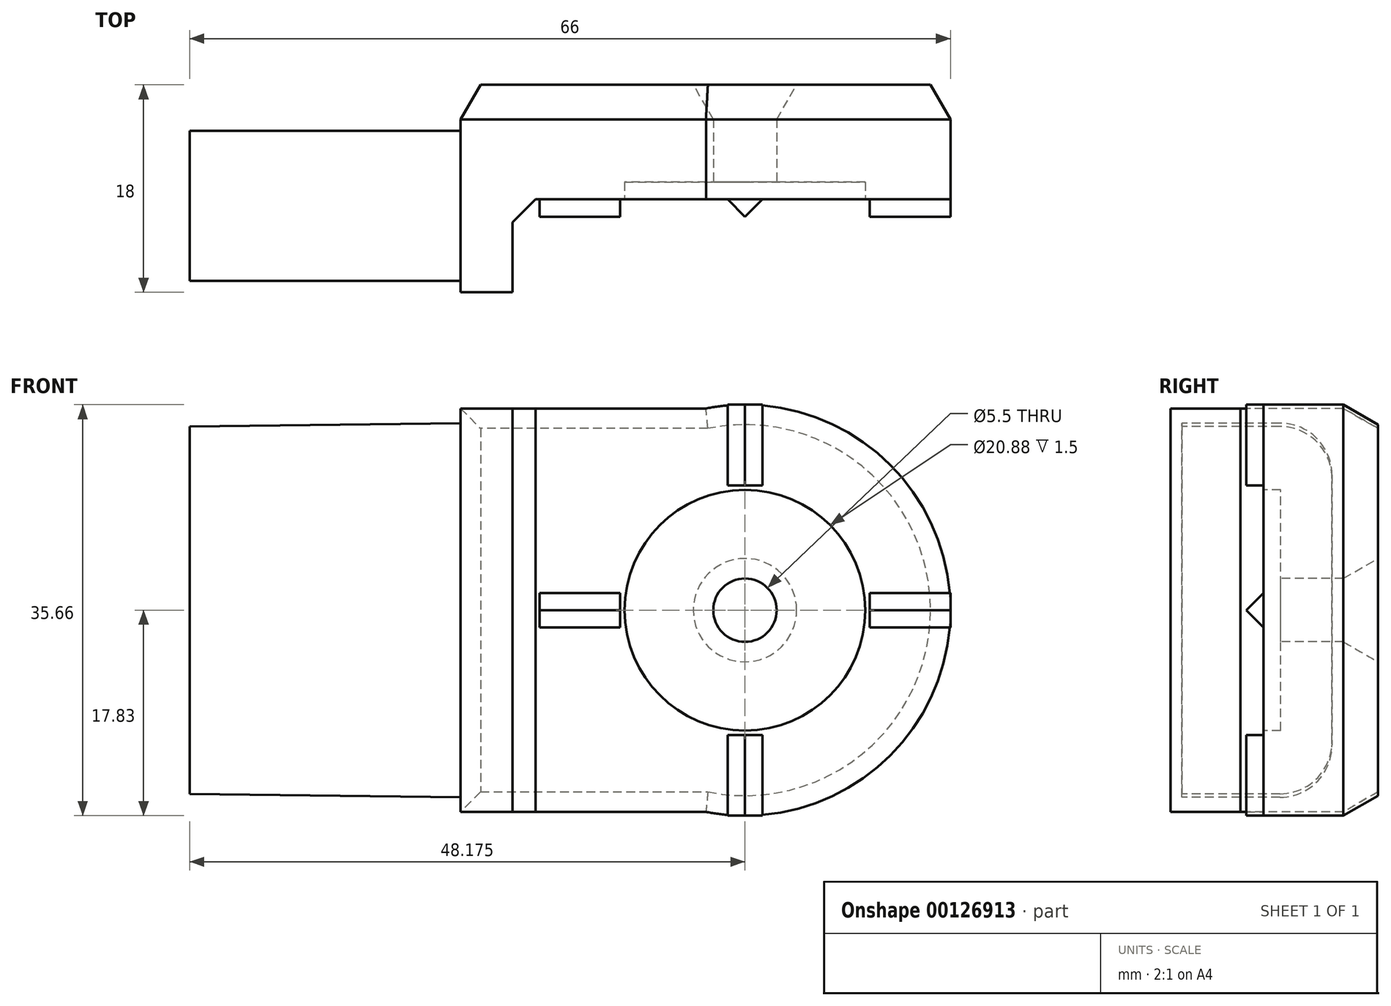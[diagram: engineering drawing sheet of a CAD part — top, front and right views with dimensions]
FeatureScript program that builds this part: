
annotation { "Feature Type Name" : "Feature", "Feature Type Description" : "" }
export const myFeature = defineFeature(function(context is Context, id is Id, definition is map)
    precondition{}
    {
        {
            var Q0;
            Q0=qCreatedBy(makeId("Front.planeOp"),FACE);
            var sketch = newSketch(context, id + "F0", { "sketchPlane" : qUnion([Q0])});
            skLineSegment(sketch, "E0.bottom", {"start": v(-32.5, 17.5) * mm, "end": v(32.5, 17.5) * mm});
            skLineSegment(sketch, "E0.top", {"start": v(-32.5, -17.5) * mm, "end": v(32.5, -17.5) * mm});
            skLineSegment(sketch, "E0.left", {"start": v(-32.5, 17.5) * mm, "end": v(-32.5, -17.5) * mm});
            skLineSegment(sketch, "E0.right", {"start": v(32.5, 17.5) * mm, "end": v(32.5, -17.5) * mm});
            skSolve(sketch);
        }
        {
            var Q0;
            Q0=makeQuery(id+"F0.imprint","IMPRINT",FACE,{"disambiguationData":[TD([[makeQuery(id+"F0.imprint","IMPRINT",EDGE,{"derivedFrom":sQuery(id+"F0.wireOp",EDGE,"E0.bottom")}),-1.0]])]});
            extrude(context, id + "F1", {"entities" : qUnion([Q0]), "depth" : 15 * mm});
        }
        {
            var Q0;
            Q0=makeQuery(id+"F1.opExtrude","CAP_FACE",FACE,{"disambiguationData":[OSD([sQuery(id+"F0.wireOp",EDGE,"E0.bottom"),sQuery(id+"F0.wireOp",EDGE,"E0.top"),sQuery(id+"F0.wireOp",EDGE,"E0.left"),sQuery(id+"F0.wireOp",EDGE,"E0.right")])],"isStart":false});
            var sketch = newSketch(context, id + "F2", { "sketchPlane" : qUnion([Q0])});
            skCircle(sketch, "E1", {"center": v(15.68, 0) * mm, "radius": 17.82 * mm});
            skSolve(sketch);
        }
        {
            var Q0;
            Q0 = qSketchRegion(id + "F2", true);
            var Q1;
            Q1=makeQuery(id+"F1.opExtrude","CAP_FACE",FACE,{"disambiguationData":[OSD([sQuery(id+"F0.wireOp",EDGE,"E0.bottom"),sQuery(id+"F0.wireOp",EDGE,"E0.top"),sQuery(id+"F0.wireOp",EDGE,"E0.left"),sQuery(id+"F0.wireOp",EDGE,"E0.right")])],"isStart":true});
            extrude(context, id + "F3", {"entities" : qUnion([Q0]), "operationType" : NewBodyOperationType.ADD, "endBound" : BoundingType.UP_TO_SURFACE, "oppositeDirection" : true, "endBoundEntityFace" : qUnion([Q1]), "depth" : 25 * mm});
        }
        {
            var Q0;
            Q0=makeQuery(id+"F3.boolean.opBoolean","MERGE",FACE,{"derivedFrom":[makeQuery(id+"F1.opExtrude","CAP_FACE",FACE,{"disambiguationData":[OSD([sQuery(id+"F0.wireOp",EDGE,"E0.bottom"),sQuery(id+"F0.wireOp",EDGE,"E0.top"),sQuery(id+"F0.wireOp",EDGE,"E0.left"),sQuery(id+"F0.wireOp",EDGE,"E0.right")])],"isStart":false}),makeQuery(id+"F3.opExtrude","CAP_FACE",FACE,{"disambiguationData":[OSD([sQuery(id+"F2.wireOp",EDGE,"E1")])],"isStart":true})]});
            var sketch = newSketch(context, id + "F4", { "sketchPlane" : qUnion([Q0])});
            skLineSegment(sketch, "E2.bottom", {"start": v(-4.5, -18.83) * mm, "end": v(34.5, -18.83) * mm});
            skLineSegment(sketch, "E2.top", {"start": v(-4.5, 18.83) * mm, "end": v(34.5, 18.83) * mm});
            skLineSegment(sketch, "E2.left", {"start": v(-4.5, -18.83) * mm, "end": v(-4.5, 18.83) * mm});
            skLineSegment(sketch, "E2.right", {"start": v(34.5, -18.83) * mm, "end": v(34.5, 18.83) * mm});
            skSolve(sketch);
        }
        {
            var Q0;
            Q0 = qSketchRegion(id + "F4", true);
            extrude(context, id + "F5", {"entities" : qUnion([Q0]), "operationType" : NewBodyOperationType.REMOVE, "oppositeDirection" : true, "depth" : 8.06 * mm});
        }
        {
            var Q0;
            Q0=makeQuery(id+"F3.boolean.opBoolean","MERGE",FACE,{"derivedFrom":[makeQuery(id+"F1.opExtrude","CAP_FACE",FACE,{"disambiguationData":[OSD([sQuery(id+"F0.wireOp",EDGE,"E0.bottom"),sQuery(id+"F0.wireOp",EDGE,"E0.top"),sQuery(id+"F0.wireOp",EDGE,"E0.left"),sQuery(id+"F0.wireOp",EDGE,"E0.right")])],"isStart":false}),makeQuery(id+"F3.opExtrude","CAP_FACE",FACE,{"disambiguationData":[OSD([sQuery(id+"F2.wireOp",EDGE,"E1")])],"isStart":true})]});
            var sketch = newSketch(context, id + "F6", { "sketchPlane" : qUnion([Q0])});
            skLineSegment(sketch, "E3", {"start": v(-9, -17.5) * mm, "end": v(-9, 17.5) * mm, "construction": true});
            skLineSegment(sketch, "E4", {"start": v(-9, 17.5) * mm, "end": v(-32.5, 17.5) * mm});
            skLineSegment(sketch, "E5", {"start": v(-32.5, 17.5) * mm, "end": v(-32.5, 15.93) * mm});
            skLineSegment(sketch, "E6", {"start": v(-32.5, 15.93) * mm, "end": v(-9, 16.23) * mm});
            skLineSegment(sketch, "E7", {"start": v(-9, 16.23) * mm, "end": v(-9, 17.5) * mm});
            skLineSegment(sketch, "E8", {"start": v(-9, -17.5) * mm, "end": v(-32.5, -17.5) * mm});
            skLineSegment(sketch, "E9", {"start": v(-32.5, -17.5) * mm, "end": v(-32.5, -15.93) * mm});
            skLineSegment(sketch, "E10", {"start": v(-32.5, -15.93) * mm, "end": v(-9, -16.23) * mm});
            skLineSegment(sketch, "E11", {"start": v(-9, -16.23) * mm, "end": v(-9, -17.5) * mm});
            skSolve(sketch);
        }
        {
            var Q0;
            Q0 = qSketchRegion(id + "F6", true);
            extrude(context, id + "F7", {"entities" : qUnion([Q0]), "operationType" : NewBodyOperationType.REMOVE, "endBound" : BoundingType.THROUGH_ALL, "oppositeDirection" : true, "depth" : 25 * mm});
        }
        {
            var Q0;
            Q0=makeQuery(id+"F3.boolean.opBoolean","MERGE",FACE,{"derivedFrom":[makeQuery(id+"F1.opExtrude","CAP_FACE",FACE,{"disambiguationData":[OSD([sQuery(id+"F0.wireOp",EDGE,"E0.bottom"),sQuery(id+"F0.wireOp",EDGE,"E0.top"),sQuery(id+"F0.wireOp",EDGE,"E0.left"),sQuery(id+"F0.wireOp",EDGE,"E0.right")])],"isStart":false}),makeQuery(id+"F3.opExtrude","CAP_FACE",FACE,{"disambiguationData":[OSD([sQuery(id+"F2.wireOp",EDGE,"E1")])],"isStart":true})]});
            var sketch = newSketch(context, id + "F8", { "sketchPlane" : qUnion([Q0])});
            skLineSegment(sketch, "E12.bottom", {"start": v(-9, -17.5) * mm, "end": v(-39.86, -17.5) * mm});
            skLineSegment(sketch, "E12.top", {"start": v(-9, 20.06) * mm, "end": v(-39.86, 20.06) * mm});
            skLineSegment(sketch, "E12.left", {"start": v(-9, -17.5) * mm, "end": v(-9, 20.06) * mm});
            skLineSegment(sketch, "E12.right", {"start": v(-39.86, -17.5) * mm, "end": v(-39.86, 20.06) * mm});
            skSolve(sketch);
        }
        {
            var Q0;
            Q0 = qSketchRegion(id + "F8", true);
            extrude(context, id + "F9", {"entities" : qUnion([Q0]), "operationType" : NewBodyOperationType.REMOVE, "oppositeDirection" : true, "depth" : 1 * mm});
        }
        {
            var Q0;
            {var subQ0=sQuery(id+"F0.wireOp",EDGE,"E0.right");var subQ1=sQuery(id+"F0.wireOp",EDGE,"E0.left");var subQ2=sQuery(id+"F0.wireOp",EDGE,"E0.top");var subQ3=sQuery(id+"F0.wireOp",EDGE,"E0.bottom");Q0=makeQuery(id+"F3.boolean.opBoolean","MERGE",FACE,{"derivedFrom":[makeQuery(id+"F1.opExtrude","CAP_FACE",FACE,{"disambiguationData":[OSD([subQ3,subQ2,subQ1,subQ0])],"isStart":true}),makeQuery(id+"F3.opExtrude","CAP_FACE",FACE,{"disambiguationData":[OSD([subQ3,subQ2,subQ1,subQ0])],"isStart":false})]});}
            var sketch = newSketch(context, id + "F10", { "sketchPlane" : qUnion([Q0])});
            skLineSegment(sketch, "E13.bottom", {"start": v(9, -17.5) * mm, "end": v(34.5, -17.5) * mm});
            skLineSegment(sketch, "E13.top", {"start": v(9, 17.5) * mm, "end": v(34.5, 17.5) * mm});
            skLineSegment(sketch, "E13.left", {"start": v(9, -17.5) * mm, "end": v(9, 17.5) * mm});
            skLineSegment(sketch, "E13.right", {"start": v(34.5, -17.5) * mm, "end": v(34.5, 17.5) * mm});
            skSolve(sketch);
        }
        {
            var Q0;
            Q0 = qSketchRegion(id + "F10", true);
            extrude(context, id + "F11", {"entities" : qUnion([Q0]), "operationType" : NewBodyOperationType.REMOVE, "oppositeDirection" : true, "depth" : 1 * mm});
        }
        {
            var Q0;
            Q0=makeQuery(id+"F5.boolean.opBoolean","COPY",EDGE,{"derivedFrom":makeQuery(id+"F5.opExtrude","CAP_EDGE",EDGE,{"disambiguationData":[OSD([sQuery(id+"F4.wireOp",EDGE,"E2.left")])],"isStart":false})});
            chamfer(context, id + "F12", {"entities" : qUnion([Q0]), "width" : 2 * mm, "tangentPropagation" : true});
        }
        {
            var Q0;
            Q0=makeQuery(id+"F5.boolean.opBoolean","COPY",FACE,{"derivedFrom":makeQuery(id+"F5.opExtrude","CAP_FACE",FACE,{"disambiguationData":[OSD([sQuery(id+"F4.wireOp",EDGE,"E2.bottom"),sQuery(id+"F4.wireOp",EDGE,"E2.top"),sQuery(id+"F4.wireOp",EDGE,"E2.left"),sQuery(id+"F4.wireOp",EDGE,"E2.right")])],"isStart":false})});
            var sketch = newSketch(context, id + "F13", { "sketchPlane" : qUnion([Q0])});
            skCircle(sketch, "E14", {"center": v(15.68, 0) * mm, "radius": 2.75 * mm});
            skSolve(sketch);
        }
        {
            var Q0;
            Q0 = qSketchRegion(id + "F13", true);
            extrude(context, id + "F14", {"entities" : qUnion([Q0]), "operationType" : NewBodyOperationType.REMOVE, "endBound" : BoundingType.THROUGH_ALL, "oppositeDirection" : true, "depth" : 25 * mm});
        }
        {
            var Q0;
            Q0=makeQuery(id+"F5.boolean.opBoolean","COPY",FACE,{"derivedFrom":makeQuery(id+"F5.opExtrude","CAP_FACE",FACE,{"disambiguationData":[OSD([sQuery(id+"F4.wireOp",EDGE,"E2.bottom"),sQuery(id+"F4.wireOp",EDGE,"E2.top"),sQuery(id+"F4.wireOp",EDGE,"E2.left"),sQuery(id+"F4.wireOp",EDGE,"E2.right")])],"isStart":false})});
            var sketch = newSketch(context, id + "F15", { "sketchPlane" : qUnion([Q0])});
            skCircle(sketch, "E15", {"center": v(15.68, 0) * mm, "radius": 10.44 * mm});
            skSolve(sketch);
        }
        {
            var Q0;
            Q0 = qSketchRegion(id + "F15", true);
            extrude(context, id + "F16", {"entities" : qUnion([Q0]), "operationType" : NewBodyOperationType.REMOVE, "oppositeDirection" : true, "depth" : 1.5 * mm});
        }
        {
            var Q0;
            Q0=makeQuery(id+"F11.boolean.opBoolean","INTERSECT",EDGE,{"derivedFrom":[makeQuery(id+"F7.boolean.opBoolean","COPY",FACE,{"derivedFrom":makeQuery(id+"F7.opExtrude","SWEPT_FACE",FACE,{"disambiguationData":[OSD([sQuery(id+"F6.wireOp",EDGE,"E6")])]})}),makeQuery(id+"F11.opExtrude","CAP_FACE",FACE,{"disambiguationData":[OSD([sQuery(id+"F10.wireOp",EDGE,"E13.bottom"),sQuery(id+"F10.wireOp",EDGE,"E13.top"),sQuery(id+"F10.wireOp",EDGE,"E13.left"),sQuery(id+"F10.wireOp",EDGE,"E13.right")])],"isStart":false})]});
            var Q1;
            Q1=makeQuery(id+"F11.boolean.opBoolean","INTERSECT",EDGE,{"derivedFrom":[makeQuery(id+"F7.boolean.opBoolean","COPY",FACE,{"derivedFrom":makeQuery(id+"F7.opExtrude","SWEPT_FACE",FACE,{"disambiguationData":[OSD([sQuery(id+"F6.wireOp",EDGE,"E10")])]})}),makeQuery(id+"F11.opExtrude","CAP_FACE",FACE,{"disambiguationData":[OSD([sQuery(id+"F10.wireOp",EDGE,"E13.bottom"),sQuery(id+"F10.wireOp",EDGE,"E13.top"),sQuery(id+"F10.wireOp",EDGE,"E13.left"),sQuery(id+"F10.wireOp",EDGE,"E13.right")])],"isStart":false})]});
            fillet(context, id + "F17", {"entities" : qUnion([Q0, Q1]), "radius" : 4.5 * mm, "tangentPropagation" : true, "allowEdgeOverflow" : false});
        }
        {
            var Q0;
            Q0=makeQuery(id+"F5.boolean.opBoolean","COPY",FACE,{"derivedFrom":makeQuery(id+"F5.opExtrude","CAP_FACE",FACE,{"disambiguationData":[OSD([sQuery(id+"F4.wireOp",EDGE,"E2.bottom"),sQuery(id+"F4.wireOp",EDGE,"E2.top"),sQuery(id+"F4.wireOp",EDGE,"E2.left"),sQuery(id+"F4.wireOp",EDGE,"E2.right")])],"isStart":false})});
            var sketch = newSketch(context, id + "F18", { "sketchPlane" : qUnion([Q0])});
            skArc(sketch, "E16", {"start": v(15.67, -17.83) * mm, "mid": v(33.5, 0) * mm, "end": v(15.68, 17.83) * mm});
            skLineSegment(sketch, "E17", {"start": v(15.68, 17.83) * mm, "end": v(15.68, 27.07) * mm});
            skLineSegment(sketch, "E18", {"start": v(15.68, 27.07) * mm, "end": v(43.45, 22.55) * mm});
            skLineSegment(sketch, "E19", {"start": v(43.45, 22.55) * mm, "end": v(39.8, -24.94) * mm});
            skLineSegment(sketch, "E20", {"start": v(39.8, -24.94) * mm, "end": v(14.35, -24.94) * mm});
            skLineSegment(sketch, "E21", {"start": v(14.35, -24.94) * mm, "end": v(15.67, -17.83) * mm});
            skSolve(sketch);
        }
        {
            var Q0;
            Q0 = qSketchRegion(id + "F18", true);
            extrude(context, id + "F19", {"entities" : qUnion([Q0]), "operationType" : NewBodyOperationType.REMOVE, "oppositeDirection" : true, "depth" : 25 * mm});
        }
        {
            var Q0;
            Q0=makeQuery(id+"F5.boolean.opBoolean","COPY",FACE,{"derivedFrom":makeQuery(id+"F5.opExtrude","CAP_FACE",FACE,{"disambiguationData":[OSD([sQuery(id+"F4.wireOp",EDGE,"E2.bottom"),sQuery(id+"F4.wireOp",EDGE,"E2.top"),sQuery(id+"F4.wireOp",EDGE,"E2.left"),sQuery(id+"F4.wireOp",EDGE,"E2.right")])],"isStart":false})});
            var sketch = newSketch(context, id + "F20", { "sketchPlane" : qUnion([Q0])});
            skLineSegment(sketch, "E22", {"start": v(15.68, 0) * mm, "end": v(45.78, 0) * mm, "construction": true});
            skLineSegment(sketch, "E23.bottom", {"start": v(26.5, 1.5) * mm, "end": v(33.5, 1.5) * mm});
            skLineSegment(sketch, "E23.top", {"start": v(26.5, -1.5) * mm, "end": v(33.5, -1.5) * mm});
            skLineSegment(sketch, "E23.left", {"start": v(26.5, 1.5) * mm, "end": v(26.5, -1.5) * mm});
            skLineSegment(sketch, "E23.right", {"start": v(33.5, 1.5) * mm, "end": v(33.5, -1.5) * mm});
            skLineSegment(sketch, "E24.1.0", {"start": v(17.18, 10.83) * mm, "end": v(17.18, 17.82) * mm});
            skLineSegment(sketch, "E24.1.1", {"start": v(14.18, 10.83) * mm, "end": v(17.18, 10.83) * mm});
            skLineSegment(sketch, "E24.1.2", {"start": v(14.18, 10.82) * mm, "end": v(14.18, 17.82) * mm});
            skLineSegment(sketch, "E24.1.3", {"start": v(14.18, 17.82) * mm, "end": v(17.18, 17.82) * mm});
            skLineSegment(sketch, "E24.2.0", {"start": v(4.85, 1.5) * mm, "end": v(-2.15, 1.5) * mm});
            skLineSegment(sketch, "E24.2.1", {"start": v(4.85, -1.5) * mm, "end": v(4.85, 1.5) * mm});
            skLineSegment(sketch, "E24.2.2", {"start": v(4.85, -1.5) * mm, "end": v(-2.15, -1.5) * mm});
            skLineSegment(sketch, "E24.2.3", {"start": v(-2.15, -1.5) * mm, "end": v(-2.15, 1.5) * mm});
            skLineSegment(sketch, "E24.3.0", {"start": v(14.18, -10.83) * mm, "end": v(14.18, -17.82) * mm});
            skLineSegment(sketch, "E24.3.1", {"start": v(17.18, -10.83) * mm, "end": v(14.18, -10.83) * mm});
            skLineSegment(sketch, "E24.3.2", {"start": v(17.18, -10.82) * mm, "end": v(17.18, -17.83) * mm});
            skLineSegment(sketch, "E24.3.3", {"start": v(17.18, -17.82) * mm, "end": v(14.18, -17.82) * mm});
            skPoint(sketch, "E24.center", {"position": v(15.68, 0) * mm});
            skSolve(sketch);
        }
        {
            var Q0;
            Q0 = qSketchRegion(id + "F20", true);
            extrude(context, id + "F21", {"entities" : qUnion([Q0]), "operationType" : NewBodyOperationType.ADD, "depth" : 1.7 * mm});
        }
        {
            var Q0;
            Q0=makeQuery(id+"F21.opExtrude","CAP_EDGE",EDGE,{"disambiguationData":[OSD([sQuery(id+"F20.wireOp",EDGE,"E23.bottom")])],"isStart":false});
            var Q1;
            Q1=makeQuery(id+"F21.opExtrude","CAP_EDGE",EDGE,{"disambiguationData":[OSD([sQuery(id+"F20.wireOp",EDGE,"E23.top")])],"isStart":false});
            var Q2;
            Q2=makeQuery(id+"F21.opExtrude","CAP_EDGE",EDGE,{"disambiguationData":[OSD([sQuery(id+"F20.wireOp",EDGE,"E24.3.2")])],"isStart":false});
            var Q3;
            Q3=makeQuery(id+"F21.opExtrude","CAP_EDGE",EDGE,{"disambiguationData":[OSD([sQuery(id+"F20.wireOp",EDGE,"E24.3.0")])],"isStart":false});
            var Q4;
            Q4=makeQuery(id+"F21.opExtrude","CAP_EDGE",EDGE,{"disambiguationData":[OSD([sQuery(id+"F20.wireOp",EDGE,"E24.2.2")])],"isStart":false});
            var Q5;
            Q5=makeQuery(id+"F21.opExtrude","CAP_EDGE",EDGE,{"disambiguationData":[OSD([sQuery(id+"F20.wireOp",EDGE,"E24.2.0")])],"isStart":false});
            var Q6;
            Q6=makeQuery(id+"F21.opExtrude","CAP_EDGE",EDGE,{"disambiguationData":[OSD([sQuery(id+"F20.wireOp",EDGE,"E24.1.2")])],"isStart":false});
            var Q7;
            Q7=makeQuery(id+"F21.opExtrude","CAP_EDGE",EDGE,{"disambiguationData":[OSD([sQuery(id+"F20.wireOp",EDGE,"E24.1.0")])],"isStart":false});
            chamfer(context, id + "F22", {"entities" : qUnion([Q0, Q1, Q2, Q3, Q4, Q5, Q6, Q7]), "width" : 1.7 * mm, "tangentPropagation" : true});
        }
        {
            var Q0;
            {var subQ0=sQuery(id+"F0.wireOp",EDGE,"E0.right");var subQ1=sQuery(id+"F0.wireOp",EDGE,"E0.left");var subQ2=sQuery(id+"F0.wireOp",EDGE,"E0.top");var subQ3=sQuery(id+"F0.wireOp",EDGE,"E0.bottom");Q0=makeQuery(id+"F3.boolean.opBoolean","MERGE",FACE,{"derivedFrom":[makeQuery(id+"F1.opExtrude","CAP_FACE",FACE,{"disambiguationData":[OSD([subQ3,subQ2,subQ1,subQ0])],"isStart":true}),makeQuery(id+"F3.opExtrude","CAP_FACE",FACE,{"disambiguationData":[OSD([subQ3,subQ2,subQ1,subQ0])],"isStart":false})]});}
            extrude(context, id + "F23", {"entities" : qUnion([Q0]), "operationType" : NewBodyOperationType.ADD, "depth" : 3 * mm, "hasDraft" : true, "draftAngle" : 30 * degree, "draftPullDirection" : true});
        }
    });
